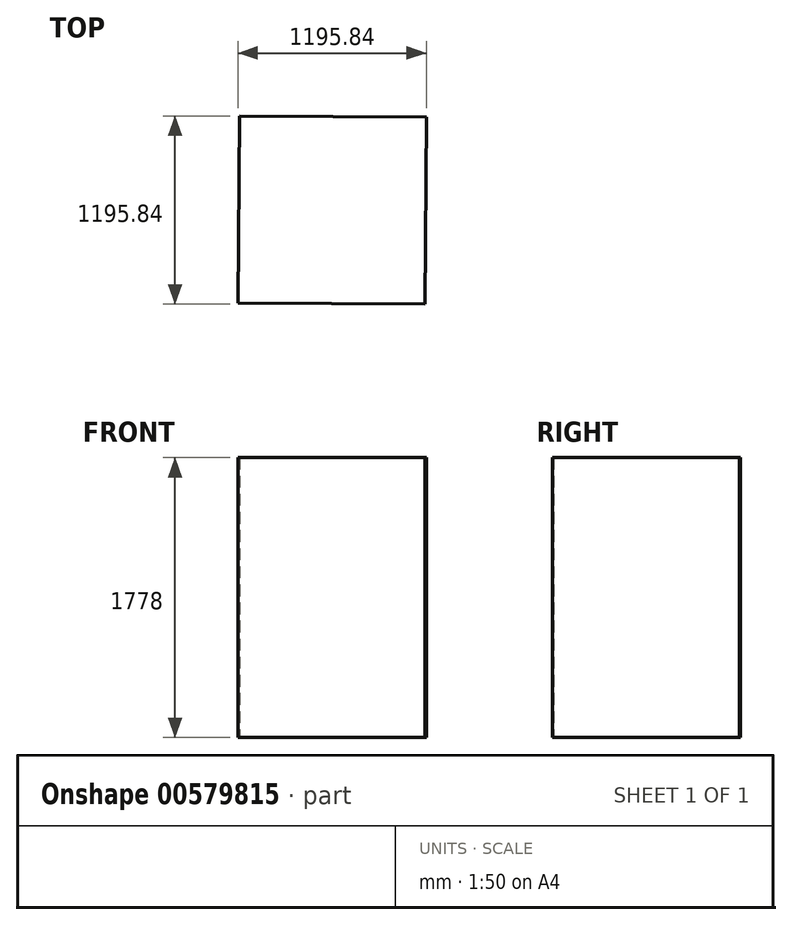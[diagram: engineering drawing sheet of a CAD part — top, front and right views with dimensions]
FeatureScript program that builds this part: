
annotation { "Feature Type Name" : "Feature", "Feature Type Description" : "" }
export const myFeature = defineFeature(function(context is Context, id is Id, definition is map)
    precondition{}
    {
        {
            var Q0;
            Q0=qCreatedBy(makeId("Top.planeOp"),FACE);
            var sketch = newSketch(context, id + "F0", { "sketchPlane" : qUnion([Q0])});
            skCircle(sketch, "E0.cCircle", {"center": v(0, 0) * mm, "radius": 593.9 * mm, "construction": true});
            skLineSegment(sketch, "E0.0", {"start": v(597.92, 589.86) * mm, "end": v(589.86, -597.92) * mm});
            skLineSegment(sketch, "E0.1", {"start": v(589.86, -597.92) * mm, "end": v(-597.92, -589.86) * mm});
            skLineSegment(sketch, "E0.2", {"start": v(-597.92, -589.86) * mm, "end": v(-589.86, 597.92) * mm});
            skLineSegment(sketch, "E0.3", {"start": v(-589.86, 597.92) * mm, "end": v(597.92, 589.86) * mm});
            skPoint(sketch, "E0.0.midPoint", {"position": v(593.89, -4.03) * mm});
            skSolve(sketch);
        }
        {
            var Q0;
            Q0 = qSketchRegion(id + "F0", true);
            extrude(context, id + "F1", {"entities" : qUnion([Q0]), "depth" : 1778 * mm, "offsetDistance" : 25.4 * mm});
        }
    });
